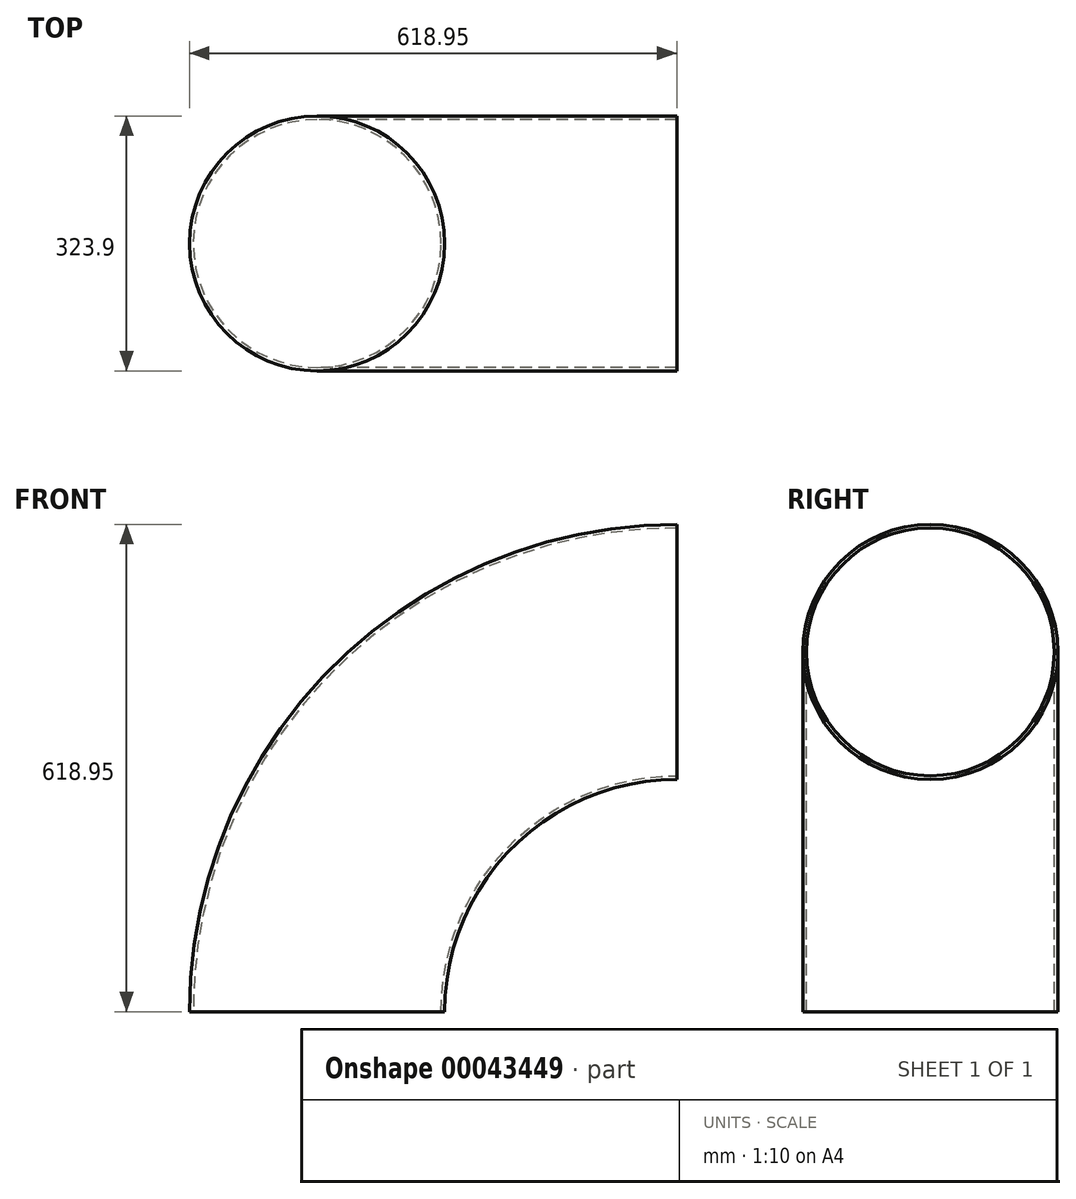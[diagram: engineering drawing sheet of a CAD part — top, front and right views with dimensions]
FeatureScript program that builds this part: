
annotation { "Feature Type Name" : "Feature", "Feature Type Description" : "" }
export const myFeature = defineFeature(function(context is Context, id is Id, definition is map)
    precondition{}
    {
        {
            var Q0;
            Q0=qCreatedBy(makeId("Front.planeOp"),FACE);
            var sketch = newSketch(context, id + "F0", { "sketchPlane" : qUnion([Q0])});
            skLineSegment(sketch, "E0", {"start": v(0, 0) * mm, "end": v(-457, 0) * mm, "construction": true});
            skLineSegment(sketch, "E1", {"start": v(0, 0) * mm, "end": v(0, 457) * mm, "construction": true});
            skArc(sketch, "E2", {"start": v(0, 457) * mm, "mid": v(-323.15, 323.15) * mm, "end": v(-457, 0) * mm});
            skSolve(sketch);
        }
        {
            var Q0;
            Q0=qCreatedBy(makeId("Top.planeOp"),FACE);
            var sketch = newSketch(context, id + "F1", { "sketchPlane" : qUnion([Q0])});
            skCircle(sketch, "E3", {"center": v(-457, 0) * mm, "radius": 161.95 * mm});
            skCircle(sketch, "E4", {"center": v(-457, 0) * mm, "radius": 157.4 * mm});
            skSolve(sketch);
        }
        {
            var Q0;
            Q0=makeQuery(id+"F1.imprint","IMPRINT",FACE,{"disambiguationData":[TD([[makeQuery(id+"F1.imprint","IMPRINT",EDGE,{"derivedFrom":sQuery(id+"F1.wireOp",EDGE,"E3")}),1.0]])]});
            var Q1;
            Q1=sQuery(id+"F0.wireOp",EDGE,"E2");
            sweep(context, id + "F2", {"profiles" : qUnion([Q0]), "path" : qUnion([Q1])});
        }
    });
